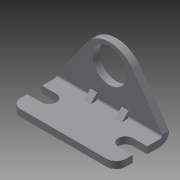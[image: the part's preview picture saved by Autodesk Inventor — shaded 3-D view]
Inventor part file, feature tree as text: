
AUTODESK INVENTOR PART (.ipt)
format: ipt  version: 2014 SP2 (Build 180246200, 246)  size: 198,144 bytes
history: native  units: in
note: dims shown in document units (in); Inventor stores cm internally (conversion verified against a paired STEP export)
features: other x126, sketch x9, extrude x8, hole x1
ambient origin geometry x8: Origin, YZ Plane, XZ Plane, XY Plane, X Axis, Y Axis, Z Axis, Center Point
bodies: Solid1 (feature_tree)
feature tree (144):
  extrude  "Extrusion1"  Depth=1.375in TaperAngle=0.0deg
  extrude  "Extrusion2"  Depth=0.375in TaperAngle=0.0deg
  hole  "Hole1"  [1 undecoded]
  extrude  "Extrusion3"  Depth=0.0897in TaperAngle=0.0deg
  extrude  "Extrusion4"  [1 undecoded]
  extrude  "Extrusion5"  [1 undecoded]
  extrude  "Extrusion6"  [1 undecoded]
  extrude  "Extrusion7"  [1 undecoded]
  extrude  "Extrusion8"  [1 undecoded]
  other  "d1_XY"
  other  "d1_YZ"
  other  "d1_ZX"
  other  "d1_X"
  other  "d1_Y"
  other  "d1_Z"
  other  "d1_Center"
  other  "d2_XY"
  other  "d2_YZ"
  other  "d2_ZX"
  other  "d2_X"
  other  "d2_Y"
  other  "d2_Z"
  other  "d2_Center"
  other  "h1_XY"
  other  "h1_YZ"
  other  "h1_ZX"
  other  "h1_X"
  other  "h1_Y"
  other  "h1_Z"
  other  "h1_Center"
  other  "h2_XY"
  other  "h2_YZ"
  other  "h2_ZX"
  other  "h2_X"
  other  "h2_Y"
  other  "h2_Z"
  other  "h2_Center"
  other  "h3_XY"
  other  "h3_YZ"
  other  "h3_ZX"
  other  "h3_X"
  other  "h3_Y"
  other  "h3_Z"
  other  "h3_Center"
  other  "h4_XY"
  other  "h4_YZ"
  other  "h4_ZX"
  other  "h4_X"
  other  "h4_Y"
  other  "h4_Z"
  other  "h4_Center"
  other  "h5_XY"
  other  "h5_YZ"
  other  "h5_ZX"
  other  "h5_X"
  other  "h5_Y"
  other  "h5_Z"
  other  "h5_Center"
  other  "h6_XY"
  other  "h6_YZ"
  other  "h6_ZX"
  other  "h6_X"
  other  "h6_Y"
  other  "h6_Z"
  other  "h6_Center"
  other  "l1_XY"
  other  "l1_YZ"
  other  "l1_ZX"
  other  "l1_X"
  other  "l1_Y"
  other  "l1_Z"
  other  "l1_Center"
  other  "l2_XY"
  other  "l2_YZ"
  other  "l2_ZX"
  other  "l2_X"
  other  "l2_Y"
  other  "l2_Z"
  other  "l2_Center"
  other  "l3_XY"
  other  "l3_YZ"
  other  "l3_ZX"
  other  "l3_X"
  other  "l3_Y"
  other  "l3_Z"
  other  "l3_Center"
  other  "l4_XY"
  other  "l4_YZ"
  other  "l4_ZX"
  other  "l4_X"
  other  "l4_Y"
  other  "l4_Z"
  other  "l4_Center"
  other  "l5_XY"
  other  "l5_YZ"
  other  "l5_ZX"
  other  "l5_X"
  other  "l5_Y"
  other  "l5_Z"
  other  "l5_Center"
  other  "l6_XY"
  other  "l6_YZ"
  other  "l6_ZX"
  other  "l6_X"
  other  "l6_Y"
  other  "l6_Z"
  other  "l6_Center"
  other  "l7_XY"
  other  "l7_YZ"
  other  "l7_ZX"
  other  "l7_X"
  other  "l7_Y"
  other  "l7_Z"
  other  "l7_Center"
  other  "l8_XY"
  other  "l8_YZ"
  other  "l8_ZX"
  other  "l8_X"
  other  "l8_Y"
  other  "l8_Z"
  other  "l8_Center"
  other  "mounting_bracket_XY"
  other  "mounting_bracket_YZ"
  other  "mounting_bracket_ZX"
  other  "mounting_bracket_X"
  other  "mounting_bracket_Y"
  other  "mounting_bracket_Z"
  other  "mounting_bracket_Center"
  other  "mounting_bracket_1_XY"
  other  "mounting_bracket_1_YZ"
  other  "mounting_bracket_1_ZX"
  other  "mounting_bracket_1_X"
  other  "mounting_bracket_1_Y"
  other  "mounting_bracket_1_Z"
  other  "mounting_bracket_1_Center"
  sketch  "Sketch_1"  dims[d0=1.375in d1=0.0in d2=0.1346in d3=0.0in]
  sketch  "Sketch_2"  dims[d4=0.4405in d5=0.75in d6=0.375in d7=0.25in d8=0.5635in d9=0.1346in d10=0.0in d11=0.1346in d12=0.0in]
  sketch  "Sketch3"  dims[d13=0.1346in d14=0.0in d15=0.1346in d16=0.0in]
  sketch  "Sketch_6"  dims[d17=0.1346in d18=0.0in d19=0.0897in d20=0.0in]
  sketch  "Sketch_7"  dims[d21=0.0897in d22=0.0in]
  sketch  "Sketch_8"  dims[d23=0.0in d24=0.0in d25=0.0in d26=0.0in d27=0.0in d28=0.0in d29=0.0in d30=0.0in d31=0.0in]
  sketch  "Sketch_9"
  sketch  "Sketch_10"
  sketch  "Sketch_14"
note: 6 required parameter values undecoded (feature->parameter linkage not recoverable at this tier; creation-order binding heuristic only, values carry confidence <= 0.55)
